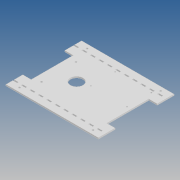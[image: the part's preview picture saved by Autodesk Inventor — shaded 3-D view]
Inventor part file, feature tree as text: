
AUTODESK INVENTOR PART (.ipt)
format: ipt  version: 2020 (Build 240168000, 168)  size: 239,616 bytes
history: native  units: mm
features: extrude x8, sketch x8, other x7, reference x6, mirror x2, pattern_linear x1
ambient origin geometry x8: Origin, YZ Plane, XZ Plane, XY Plane, X Axis, Y Axis, Z Axis, Center Point
bodies: Body1 (feature_tree)
feature tree (32):
  extrude  "Выдавливание12"  Depth=220.0mm TaperAngle=0.0deg
  mirror  "Зеркальное отражение1"
  extrude  "Выдавливание13"  Depth=3.0mm TaperAngle=0.0deg
  extrude  "Выдавливание14"  Depth=10.0mm TaperAngle=0.0deg
  extrude  "Выдавливание15"  Depth=20.0mm
  extrude  "Выдавливание16"  Depth=50.0mm
  pattern_linear  "Прямоуг.массив5"  Count1=10  [1 undecoded]
  mirror  "Зеркальное отражение2"
  sketch  "Эскиз12"
  sketch  "Эскиз13"
  sketch  "Эскиз14"
  reference  "Ссылка9"
  reference  "Ссылка10"
  sketch  "Эскиз15"
  reference  "Ссылка11"
  reference  "Ссылка12"
  reference  "Ссылка13"
  reference  "Ссылка14"
  sketch  "Эскиз16"
  sketch  "Эскиз9"
  sketch  "Эскиз10"
  sketch  "Эскиз11"
  other  "<path> - Electronic box.iam"
  other  "000.100 - Electronic box.iam"
  other  "realsenses_plate_v2.ipt:1"
  other  "realsenses_plate_2:2"
  other  "Jetson nano_fixed:1"
  other  "142-13449-1000-A02_ASM:1"
  other  "142-13449-1000-A02:1"
  extrude  "Выдавливание9"  Depth=10.0mm TaperAngle=0.0deg
  extrude  "Выдавливание10"  Depth=30.0mm
  extrude  "Выдавливание11"  Depth=10.0mm TaperAngle=0.0deg
note: 1 required parameter value undecoded (feature->parameter linkage not recoverable at this tier; creation-order binding heuristic only, values carry confidence <= 0.55)
note: 1 file-system path scrubbed to <path> (originals preserved in map.json)
